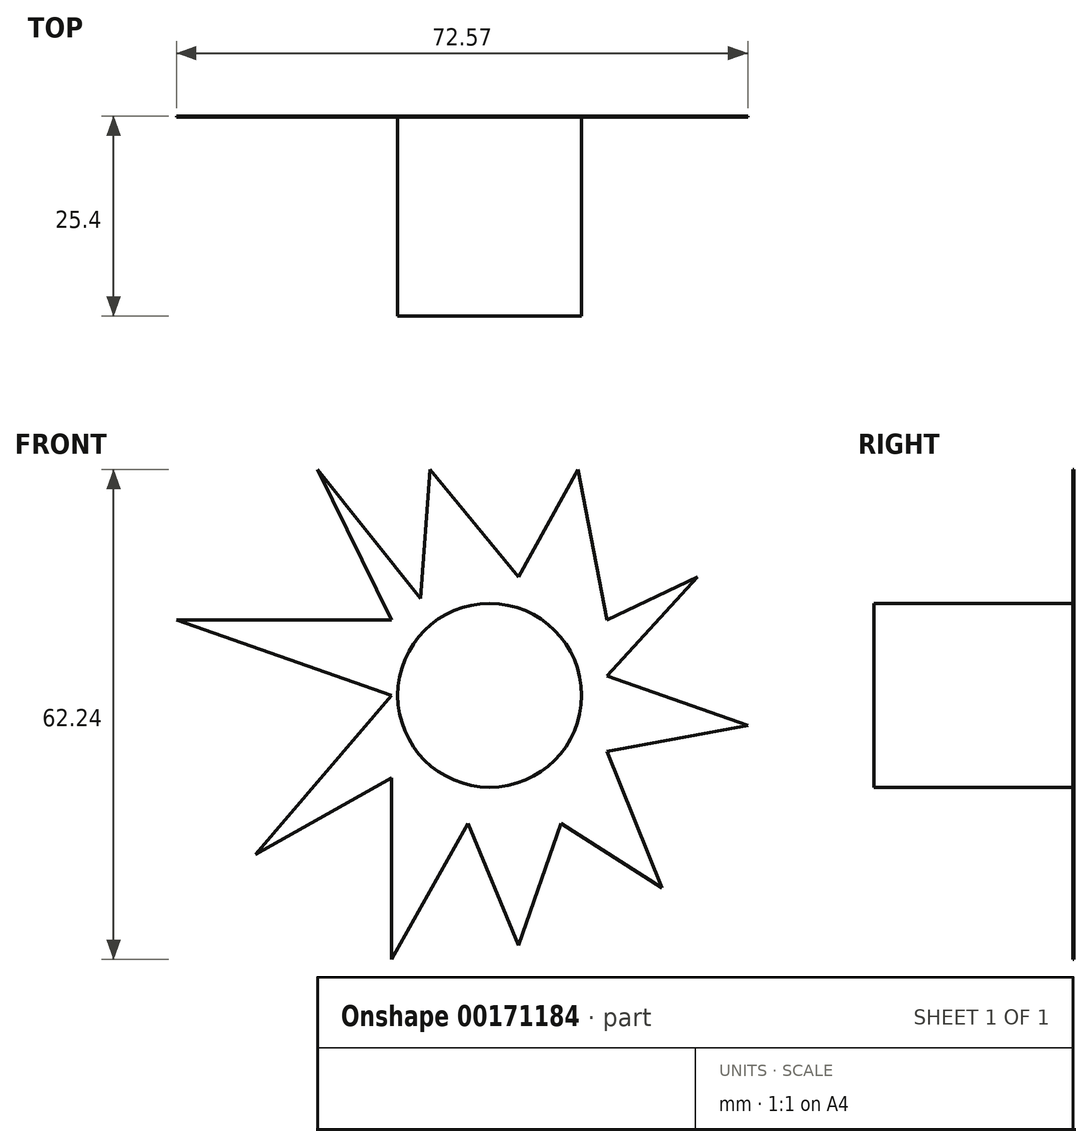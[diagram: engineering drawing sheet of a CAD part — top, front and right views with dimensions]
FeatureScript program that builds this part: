
annotation { "Feature Type Name" : "Feature", "Feature Type Description" : "" }
export const myFeature = defineFeature(function(context is Context, id is Id, definition is map)
    precondition{}
    {
        {
            var Q0;
            Q0=qCreatedBy(makeId("Front.planeOp"),FACE);
            var sketch = newSketch(context, id + "F0", { "sketchPlane" : qUnion([Q0])});
            skCircle(sketch, "E0", {"center": v(0, 0) * mm, "radius": 11.67 * mm});
            skSolve(sketch);
        }
        {
            var Q0;
            Q0=makeQuery(id+"F0.imprint","IMPRINT",FACE,{"disambiguationData":[TD([[makeQuery(id+"F0.imprint","IMPRINT",EDGE,{"derivedFrom":sQuery(id+"F0.wireOp",EDGE,"E0")}),1.0]])]});
            extrude(context, id + "F1", {"entities" : qUnion([Q0]), "depth" : 25.4 * mm});
        }
        {
            var Q0;
            Q0=qCreatedBy(makeId("Front.planeOp"),FACE);
            var sketch = newSketch(context, id + "F2", { "sketchPlane" : qUnion([Q0])});
            skLineSegment(sketch, "E1", {"start": v(-8.8, 12.3) * mm, "end": v(-21.86, 28.7) * mm});
            skLineSegment(sketch, "E2", {"start": v(-21.86, 28.7) * mm, "end": v(-12.45, 9.56) * mm});
            skLineSegment(sketch, "E3", {"start": v(-12.45, 9.56) * mm, "end": v(-39.78, 9.56) * mm});
            skLineSegment(sketch, "E4", {"start": v(-39.78, 9.56) * mm, "end": v(-12.45, 0) * mm});
            skLineSegment(sketch, "E5", {"start": v(-12.45, 0) * mm, "end": v(-29.76, -20.2) * mm});
            skLineSegment(sketch, "E6", {"start": v(-29.76, -20.2) * mm, "end": v(-12.45, -10.48) * mm});
            skLineSegment(sketch, "E7", {"start": v(-12.45, -10.48) * mm, "end": v(-12.45, -33.55) * mm});
            skLineSegment(sketch, "E8", {"start": v(-12.45, -33.55) * mm, "end": v(-2.73, -16.24) * mm});
            skLineSegment(sketch, "E9", {"start": v(-2.73, -16.24) * mm, "end": v(3.64, -31.73) * mm});
            skLineSegment(sketch, "E10", {"start": v(3.64, -31.73) * mm, "end": v(9.06, -16.24) * mm});
            skLineSegment(sketch, "E11", {"start": v(9.06, -16.24) * mm, "end": v(21.86, -24.44) * mm});
            skLineSegment(sketch, "E12", {"start": v(21.86, -24.44) * mm, "end": v(14.88, -7.14) * mm});
            skLineSegment(sketch, "E13", {"start": v(14.88, -7.14) * mm, "end": v(32.8, -3.8) * mm});
            skLineSegment(sketch, "E14", {"start": v(32.8, -3.8) * mm, "end": v(14.88, 2.47) * mm});
            skLineSegment(sketch, "E15", {"start": v(14.88, 2.47) * mm, "end": v(26.42, 15.03) * mm});
            skLineSegment(sketch, "E16", {"start": v(26.42, 15.03) * mm, "end": v(14.88, 9.56) * mm});
            skLineSegment(sketch, "E17", {"start": v(14.88, 9.56) * mm, "end": v(11.23, 28.7) * mm});
            skLineSegment(sketch, "E18", {"start": v(11.23, 28.7) * mm, "end": v(3.64, 15.03) * mm});
            skLineSegment(sketch, "E19", {"start": v(3.64, 15.03) * mm, "end": v(-7.6, 28.7) * mm});
            skLineSegment(sketch, "E20", {"start": v(-7.6, 28.7) * mm, "end": v(-8.8, 12.3) * mm});
            skSolve(sketch);
        }
        {
            var Q0;
            Q0=makeQuery(id+"F2.imprint","IMPRINT",FACE,{"disambiguationData":[TD([[makeQuery(id+"F2.imprint","IMPRINT",EDGE,{"derivedFrom":sQuery(id+"F2.wireOp",EDGE,"E1")}),1.0]])]});
            extrude(context, id + "F3", {"entities" : qUnion([Q0]), "operationType" : NewBodyOperationType.ADD, "depth" : 0.13 * mm});
        }
    });
